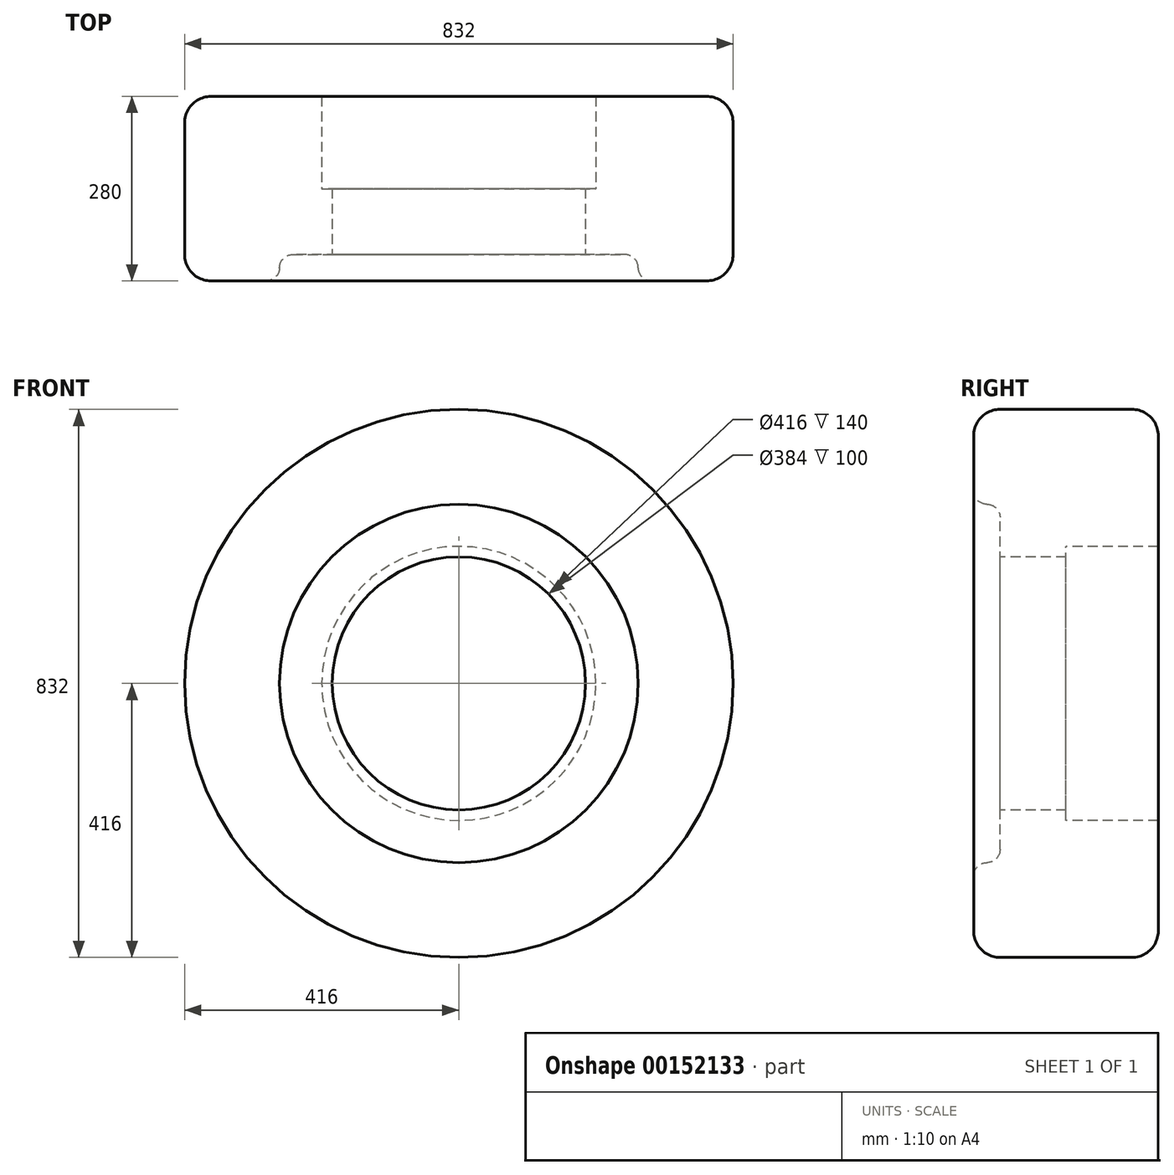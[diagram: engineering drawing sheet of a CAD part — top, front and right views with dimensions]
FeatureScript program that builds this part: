
annotation { "Feature Type Name" : "Feature", "Feature Type Description" : "" }
export const myFeature = defineFeature(function(context is Context, id is Id, definition is map)
    precondition{}
    {
        {
            var Q0;
            Q0=qCreatedBy(makeId("Top.planeOp"),FACE);
            var sketch = newSketch(context, id + "F0", { "sketchPlane" : qUnion([Q0])});
            skLineSegment(sketch, "E0", {"start": v(0, 0) * mm, "end": v(0, 6.54) * mm, "construction": true});
            skLineSegment(sketch, "E1", {"start": v(5.2, 0) * mm, "end": v(5.2, -3.5) * mm});
            skLineSegment(sketch, "E2", {"start": v(4.8, -3.5) * mm, "end": v(5.2, -3.5) * mm});
            skLineSegment(sketch, "E3", {"start": v(4.8, -3.5) * mm, "end": v(4.8, -6) * mm});
            skLineSegment(sketch, "E4", {"start": v(7.3, -7) * mm, "end": v(9.4, -7) * mm});
            skLineSegment(sketch, "E5", {"start": v(5.2, 0) * mm, "end": v(9.4, 0) * mm});
            skLineSegment(sketch, "E6", {"start": v(10.4, -1) * mm, "end": v(10.4, -6) * mm});
            skPoint(sketch, "E7.visualSharp", {"position": v(10.4, 0) * mm});
            skArc(sketch, "E7.filletArc", {"start": v(10.4, -1) * mm, "mid": v(10.1, -0.3) * mm, "end": v(9.4, 0) * mm});
            skPoint(sketch, "E8.visualSharp", {"position": v(10.4, -7) * mm});
            skArc(sketch, "E8.filletArc", {"start": v(9.4, -7) * mm, "mid": v(10.1, -6.7) * mm, "end": v(10.4, -6) * mm});
            skLineSegment(sketch, "E9", {"start": v(4.8, -6) * mm, "end": v(6.3, -6) * mm});
            skLineSegment(sketch, "E10", {"start": v(6.8, -6.5) * mm, "end": v(6.8, -6.5) * mm});
            skPoint(sketch, "E11.visualSharp", {"position": v(6.8, -7) * mm});
            skArc(sketch, "E11.filletArc", {"start": v(6.8, -6.5) * mm, "mid": v(6.95, -6.85) * mm, "end": v(7.3, -7) * mm});
            skPoint(sketch, "E12.visualSharp", {"position": v(6.8, -6) * mm});
            skArc(sketch, "E12.filletArc", {"start": v(6.8, -6.5) * mm, "mid": v(6.65, -6.15) * mm, "end": v(6.3, -6) * mm});
            skSolve(sketch);
        }
        {
            var Q0;
            Q0=qSketchRegion(id+"F0",true);
            var Q1;
            Q1=sQuery(id+"F0.wireOp",EDGE,"E0");
            revolve(context, id + "F1", {"entities" : qUnion([Q0]), "axis" : qUnion([Q1]), "revolveType" : RevolveType.FULL});
        }
        {
            var Q0;
            Q0=makeQuery(id+"F1.opRevolve","SWEPT_BODY",BODY,{"disambiguationData":[OSD([sQuery(id+"F0.wireOp",EDGE,"E1"),sQuery(id+"F0.wireOp",EDGE,"E2"),sQuery(id+"F0.wireOp",EDGE,"E3"),sQuery(id+"F0.wireOp",EDGE,"E4"),sQuery(id+"F0.wireOp",EDGE,"E5"),sQuery(id+"F0.wireOp",EDGE,"E6"),sQuery(id+"F0.wireOp",EDGE,"E7.filletArc"),sQuery(id+"F0.wireOp",EDGE,"E8.filletArc"),sQuery(id+"F0.wireOp",EDGE,"E9"),sQuery(id+"F0.wireOp",EDGE,"E11.filletArc"),sQuery(id+"F0.wireOp",EDGE,"E12.filletArc")])]});
            var Q1;
            Q1=qCreatedBy(makeId("Origin.pointOp"),VERTEX);
            transform(context, id + "F2", {"entities" : qUnion([Q0]), "transformType" : TransformType.SCALE_UNIFORMLY, "scale" : 40, "scalePoint" : qUnion([Q1]), "makeCopy" : false});
        }
    });
